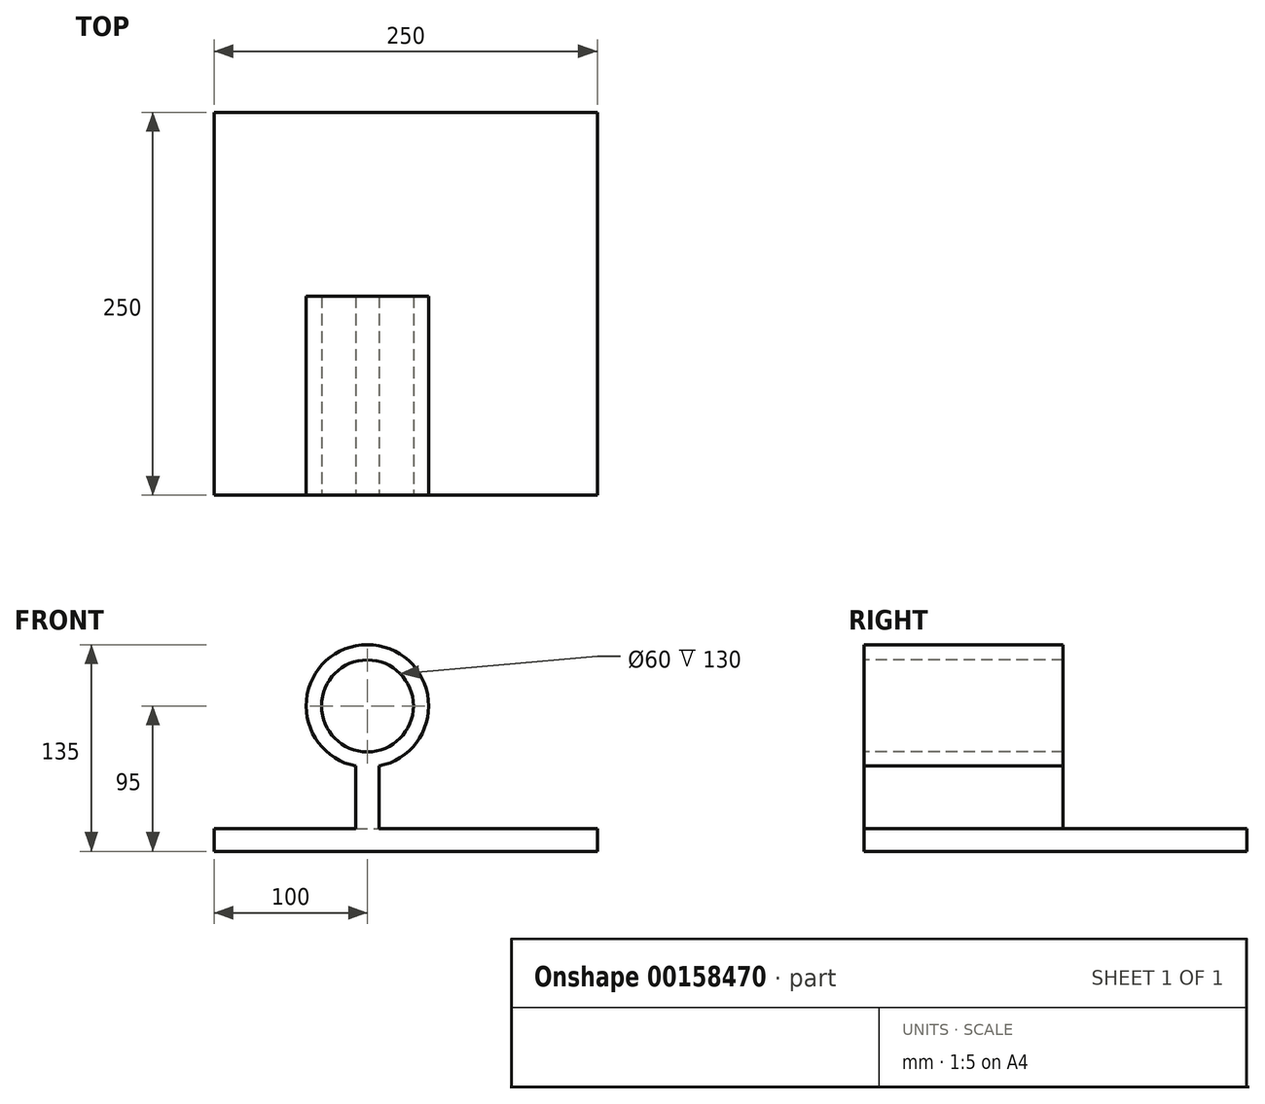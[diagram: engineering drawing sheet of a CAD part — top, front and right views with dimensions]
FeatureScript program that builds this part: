
annotation { "Feature Type Name" : "Feature", "Feature Type Description" : "" }
export const myFeature = defineFeature(function(context is Context, id is Id, definition is map)
    precondition{}
    {
        {
            var Q0;
            Q0=qCreatedBy(makeId("Top.planeOp"),FACE);
            var sketch = newSketch(context, id + "F0", { "sketchPlane" : qUnion([Q0])});
            skLineSegment(sketch, "E0.bottom", {"start": v(-125, -125) * mm, "end": v(125, -125) * mm});
            skLineSegment(sketch, "E0.top", {"start": v(-125, 125) * mm, "end": v(125, 125) * mm});
            skLineSegment(sketch, "E0.left", {"start": v(-125, -125) * mm, "end": v(-125, 125) * mm});
            skLineSegment(sketch, "E0.right", {"start": v(125, -125) * mm, "end": v(125, 125) * mm});
            skPoint(sketch, "E0.middle", {"position": v(0, 0) * mm});
            skSolve(sketch);
        }
        {
            var Q0;
            Q0=makeQuery(id+"F0.imprint","IMPRINT",FACE,{"disambiguationData":[TD([[makeQuery(id+"F0.imprint","IMPRINT",EDGE,{"derivedFrom":sQuery(id+"F0.wireOp",EDGE,"E0.bottom")}),1.0]])]});
            extrude(context, id + "F1", {"entities" : qUnion([Q0]), "depth" : 15 * mm});
        }
        {
            var Q0;
            Q0=makeQuery(id+"F1.opExtrude","SWEPT_FACE",FACE,{"disambiguationData":[OSD([sQuery(id+"F0.wireOp",EDGE,"E0.bottom")])]});
            var sketch = newSketch(context, id + "F2", { "sketchPlane" : qUnion([Q0])});
            skLineSegment(sketch, "E1", {"start": v(-25, 0) * mm, "end": v(-25, 139.07) * mm, "construction": true});
            skArc(sketch, "E2", {"start": v(-17.5, 55.7) * mm, "mid": v(-25, 135) * mm, "end": v(-32.5, 55.7) * mm});
            skCircle(sketch, "E3", {"center": v(-25, 95) * mm, "radius": 30 * mm});
            skLineSegment(sketch, "E4", {"start": v(-32.5, 0) * mm, "end": v(-32.5, 55.7) * mm});
            skLineSegment(sketch, "E5", {"start": v(-17.5, 0) * mm, "end": v(-17.5, 55.7) * mm});
            skLineSegment(sketch, "E6", {"start": v(-32.5, 0) * mm, "end": v(-17.5, 0) * mm});
            skSolve(sketch);
        }
        {
            var Q0;
            {var subQ1=sQuery(id+"F2.wireOp",EDGE,"E2");Q0=makeQuery(id+"F2.imprint","IMPRINT",FACE,{"disambiguationData":[TD([[makeQuery(id+"F2.imprint","IMPRINT",EDGE,{"derivedFrom":subQ1}),1.0]])]});}
            extrude(context, id + "F3", {"entities" : qUnion([Q0]), "operationType" : NewBodyOperationType.ADD, "oppositeDirection" : true, "depth" : 130 * mm});
        }
    });
